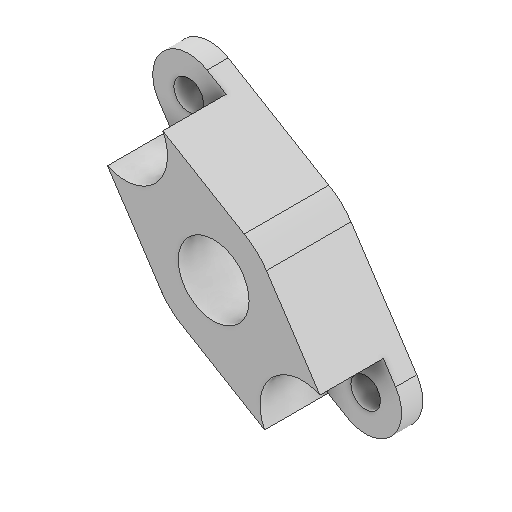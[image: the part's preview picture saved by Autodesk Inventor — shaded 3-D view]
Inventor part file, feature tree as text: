
AUTODESK INVENTOR PART (.ipt)
format: ipt  version: 2022 (Build 260153000, 153)  size: 156,160 bytes
history: native  units: mm
features: reference x6, sketch x4, extrude x3, other x2, hole x1, projected_geometry x1
ambient origin geometry x8: Origin, YZ Plane, XZ Plane, XY Plane, X Axis, Y Axis, Z Axis, Center Point
bodies: Volumenkörper1 (feature_tree)
feature tree (17):
  extrude  "Extrusion1"  Depth=2.0mm
  extrude  "Extrusion2"  Depth=6.7mm
  extrude  "Extrusion3"  [1 undecoded]
  hole  "Bohrung1"  [1 undecoded]
  sketch  "Skizze1"  dims[d0=8.0mm d1=0.0mm d2=2.0mm]
  reference  "Referenz1"
  reference  "Referenz2"
  reference  "Referenz3"
  sketch  "Skizze2"  dims[d3=3.0mm d4=0.0mm d5=6.7mm]
  projected_geometry  "Projizierte Kontur1"
  sketch  "Skizze3"  dims[d6=3.0mm d7=0.0mm]
  reference  "Referenz4"
  reference  "Referenz5"
  reference  "Referenz6"
  sketch  "Skizze4"  dims[d8=2.8mm d9=6.0mm d10=8.0mm d11=6.0mm d12=90.0deg d13=8.0mm d14=20.594885mm]
  other  "Assembly_Matchboxscope_injectionmolded.iam"
  other  "IM_Matchboxscope_base:1"
note: 2 required parameter values undecoded (feature->parameter linkage not recoverable at this tier; creation-order binding heuristic only, values carry confidence <= 0.55)
